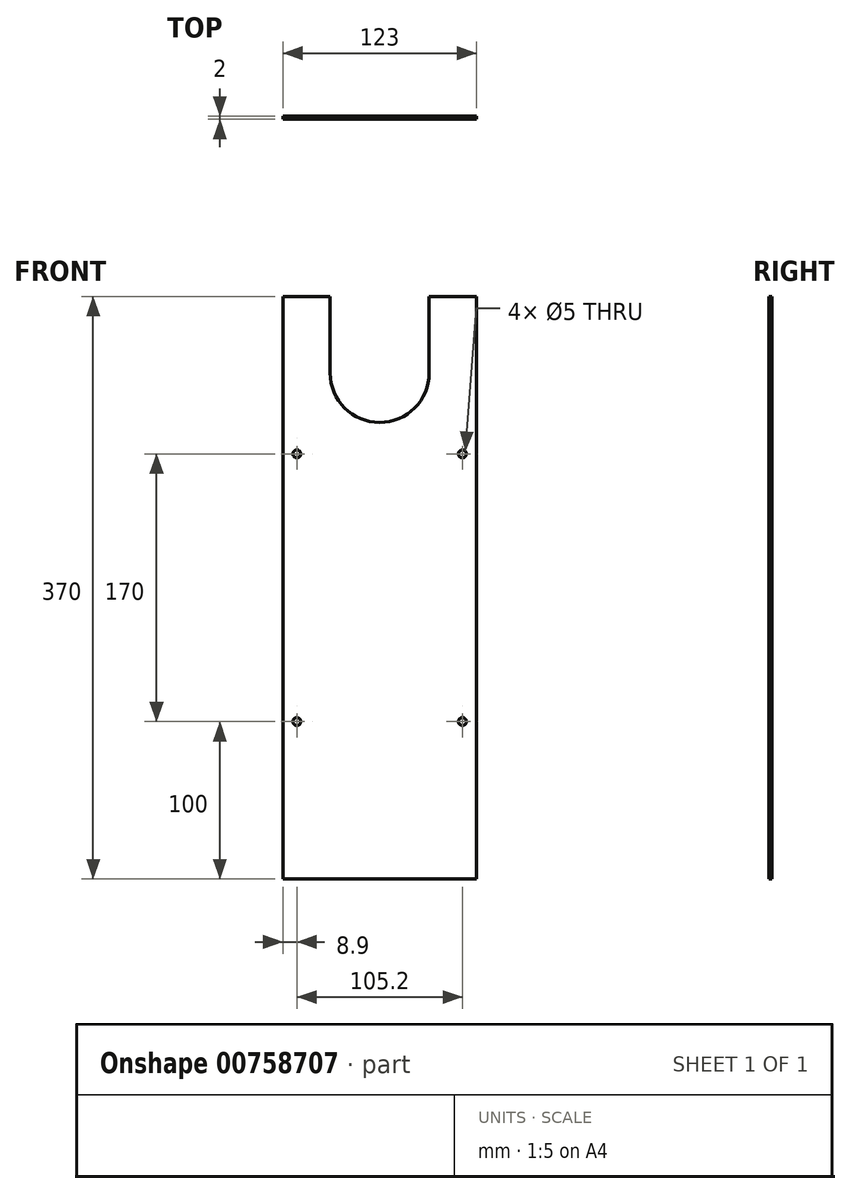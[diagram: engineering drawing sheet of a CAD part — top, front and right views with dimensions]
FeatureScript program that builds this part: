
annotation { "Feature Type Name" : "Feature", "Feature Type Description" : "" }
export const myFeature = defineFeature(function(context is Context, id is Id, definition is map)
    precondition{}
    {
        {
            var Q0;
            Q0=qCreatedBy(makeId("Front.planeOp"),FACE);
            var sketch = newSketch(context, id + "F0", { "sketchPlane" : qUnion([Q0])});
            skLineSegment(sketch, "E0.bottom", {"start": v(0, 0) * mm, "end": v(61.5, 0) * mm});
            skLineSegment(sketch, "E0.top", {"start": v(31.5, 370) * mm, "end": v(61.5, 370) * mm});
            skLineSegment(sketch, "E0.right", {"start": v(61.5, 0) * mm, "end": v(61.5, 370) * mm});
            skLineSegment(sketch, "E1.top", {"start": v(-5.5, 290) * mm, "end": v(31.5, 290) * mm});
            skLineSegment(sketch, "E1.right", {"start": v(31.5, 370) * mm, "end": v(31.5, 290) * mm});
            skCircle(sketch, "E2", {"center": v(-52.6, 100) * mm, "radius": 2.5 * mm});
            skCircle(sketch, "E3", {"center": v(-52.6, 270) * mm, "radius": 2.5 * mm});
            skLineSegment(sketch, "E4", {"start": v(0, 0) * mm, "end": v(0, 452.98) * mm, "construction": true});
            skCircle(sketch, "E5.MirrorC", {"center": v(52.6, 100) * mm, "radius": 2.5 * mm});
            skCircle(sketch, "E6.MirrorC", {"center": v(52.6, 270) * mm, "radius": 2.5 * mm});
            skLineSegment(sketch, "E7.MirrorCS", {"start": v(-61.5, 0) * mm, "end": v(-61.5, 370) * mm});
            skLineSegment(sketch, "E8.MirrorCS", {"start": v(-31.5, 370) * mm, "end": v(-61.5, 370) * mm});
            skLineSegment(sketch, "E9.MirrorCS", {"start": v(-31.5, 370) * mm, "end": v(-31.5, 290) * mm});
            skLineSegment(sketch, "E10.MirrorCS", {"start": v(5.5, 290) * mm, "end": v(-31.5, 290) * mm});
            skLineSegment(sketch, "E11.MirrorCS", {"start": v(0, 0) * mm, "end": v(-61.5, 0) * mm});
            skSolve(sketch);
        }
        {
            var Q0;
            Q0 = qSketchRegion(id + "F0", true);
            extrude(context, id + "F1", {"entities" : qUnion([Q0]), "depth" : 2 * mm, "offsetDistance" : 25 * mm});
        }
        {
            var Q0;
            Q0=makeQuery(id+"F1.opExtrude","SWEPT_EDGE",EDGE,{"disambiguationData":[OSD([sQuery(id+"F0.wireOp",EDGE,"E9.MirrorCS"),sQuery(id+"F0.wireOp",EDGE,"E10.MirrorCS")])]});
            var Q1;
            Q1=makeQuery(id+"F1.opExtrude","SWEPT_EDGE",EDGE,{"disambiguationData":[OSD([sQuery(id+"F0.wireOp",EDGE,"E1.top"),sQuery(id+"F0.wireOp",EDGE,"E1.right")])]});
            fillet(context, id + "F2", {"entities" : qUnion([Q0, Q1]), "radius" : (63 / 2) * mm, "tangentPropagation" : true, "allowEdgeOverflow" : false});
        }
    });
